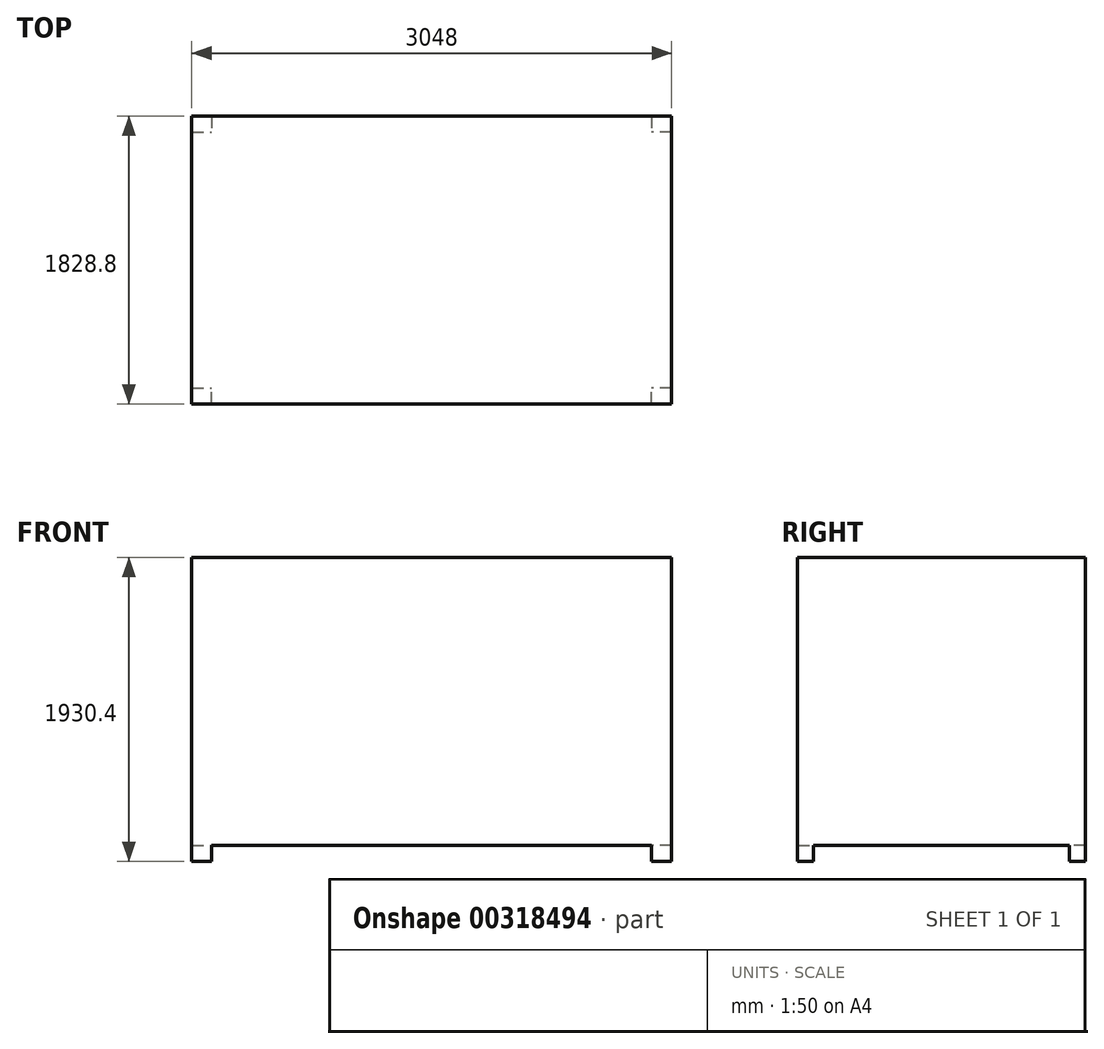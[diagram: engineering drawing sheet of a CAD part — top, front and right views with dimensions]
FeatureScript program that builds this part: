
annotation { "Feature Type Name" : "Feature", "Feature Type Description" : "" }
export const myFeature = defineFeature(function(context is Context, id is Id, definition is map)
    precondition{}
    {
        {
            var Q0;
            Q0=qCreatedBy(makeId("Top.planeOp"),FACE);
            var sketch = newSketch(context, id + "F0", { "sketchPlane" : qUnion([Q0])});
            skLineSegment(sketch, "E0", {"start": v(-4898.02, 0) * mm, "end": v(5565.8, 0) * mm, "construction": true});
            skLineSegment(sketch, "E1", {"start": v(0, 4990.62) * mm, "end": v(0, -7015.22) * mm, "construction": true});
            skPoint(sketch, "E2.middle", {"position": v(0, 0) * mm});
            skLineSegment(sketch, "E3.bottom", {"start": v(1524, 914.4) * mm, "end": v(-1524, 914.4) * mm});
            skLineSegment(sketch, "E3.top", {"start": v(1524, -914.4) * mm, "end": v(-1524, -914.4) * mm});
            skLineSegment(sketch, "E3.left", {"start": v(1524, 914.4) * mm, "end": v(1524, -914.4) * mm});
            skLineSegment(sketch, "E3.right", {"start": v(-1524, 914.4) * mm, "end": v(-1524, -914.4) * mm});
            skSolve(sketch);
        }
        {
            var Q0;
            Q0=makeQuery(id+"F0.imprint","IMPRINT",FACE,{"disambiguationData":[TD([[makeQuery(id+"F0.imprint","IMPRINT",EDGE,{"derivedFrom":sQuery(id+"F0.wireOp",EDGE,"E3.bottom")}),1.0]])]});
            extrude(context, id + "F1", {"entities" : qUnion([Q0]), "endBound" : BoundingType.SYMMETRIC, "depth" : 1828.8 * mm});
        }
        {
            var Q0;
            Q0=makeQuery(id+"F1.opExtrude","CAP_FACE",FACE,{"disambiguationData":[OSD([sQuery(id+"F0.wireOp",EDGE,"E3.bottom"),sQuery(id+"F0.wireOp",EDGE,"E3.top"),sQuery(id+"F0.wireOp",EDGE,"E3.left"),sQuery(id+"F0.wireOp",EDGE,"E3.right")])],"isStart":true});
            var sketch = newSketch(context, id + "F2", { "sketchPlane" : qUnion([Q0])});
            skLineSegment(sketch, "E4.bottom", {"start": v(-1524, 914.4) * mm, "end": v(-1397, 914.4) * mm});
            skLineSegment(sketch, "E4.top", {"start": v(-1524, 812.8) * mm, "end": v(-1397, 812.8) * mm});
            skLineSegment(sketch, "E4.left", {"start": v(-1524, 914.4) * mm, "end": v(-1524, 812.8) * mm});
            skLineSegment(sketch, "E4.right", {"start": v(-1397, 914.4) * mm, "end": v(-1397, 812.8) * mm});
            skLineSegment(sketch, "E5.bottom", {"start": v(1524, 914.4) * mm, "end": v(1397, 914.4) * mm});
            skLineSegment(sketch, "E5.top", {"start": v(1524, 812.8) * mm, "end": v(1397, 812.8) * mm});
            skLineSegment(sketch, "E5.left", {"start": v(1524, 914.4) * mm, "end": v(1524, 812.8) * mm});
            skLineSegment(sketch, "E5.right", {"start": v(1397, 914.4) * mm, "end": v(1397, 812.8) * mm});
            skLineSegment(sketch, "E6.bottom", {"start": v(1524, -914.4) * mm, "end": v(1397, -914.4) * mm});
            skLineSegment(sketch, "E6.top", {"start": v(1524, -812.8) * mm, "end": v(1397, -812.8) * mm});
            skLineSegment(sketch, "E6.left", {"start": v(1524, -914.4) * mm, "end": v(1524, -812.8) * mm});
            skLineSegment(sketch, "E6.right", {"start": v(1397, -914.4) * mm, "end": v(1397, -812.8) * mm});
            skLineSegment(sketch, "E7.bottom", {"start": v(-1524, -914.4) * mm, "end": v(-1397, -914.4) * mm});
            skLineSegment(sketch, "E7.top", {"start": v(-1524, -812.8) * mm, "end": v(-1397, -812.8) * mm});
            skLineSegment(sketch, "E7.left", {"start": v(-1524, -914.4) * mm, "end": v(-1524, -812.8) * mm});
            skLineSegment(sketch, "E7.right", {"start": v(-1397, -914.4) * mm, "end": v(-1397, -812.8) * mm});
            skSolve(sketch);
        }
        {
            var Q0;
            Q0=makeQuery(id+"F2.imprint","IMPRINT",FACE,{"disambiguationData":[TD([[makeQuery(id+"F2.imprint","IMPRINT",EDGE,{"derivedFrom":sQuery(id+"F2.wireOp",EDGE,"E4.bottom")}),1.0]])]});
            var Q1;
            Q1=makeQuery(id+"F2.imprint","IMPRINT",FACE,{"disambiguationData":[TD([[makeQuery(id+"F2.imprint","IMPRINT",EDGE,{"derivedFrom":sQuery(id+"F2.wireOp",EDGE,"E7.bottom")}),-1.0]])]});
            var Q2;
            Q2=makeQuery(id+"F2.imprint","IMPRINT",FACE,{"disambiguationData":[TD([[makeQuery(id+"F2.imprint","IMPRINT",EDGE,{"derivedFrom":sQuery(id+"F2.wireOp",EDGE,"E6.bottom")}),-1.0]])]});
            var Q3;
            Q3=makeQuery(id+"F2.imprint","IMPRINT",FACE,{"disambiguationData":[TD([[makeQuery(id+"F2.imprint","IMPRINT",EDGE,{"derivedFrom":sQuery(id+"F2.wireOp",EDGE,"E5.bottom")}),1.0]])]});
            extrude(context, id + "F3", {"entities" : qUnion([Q0, Q1, Q2, Q3]), "operationType" : NewBodyOperationType.ADD, "depth" : 101.6 * mm});
        }
    });
